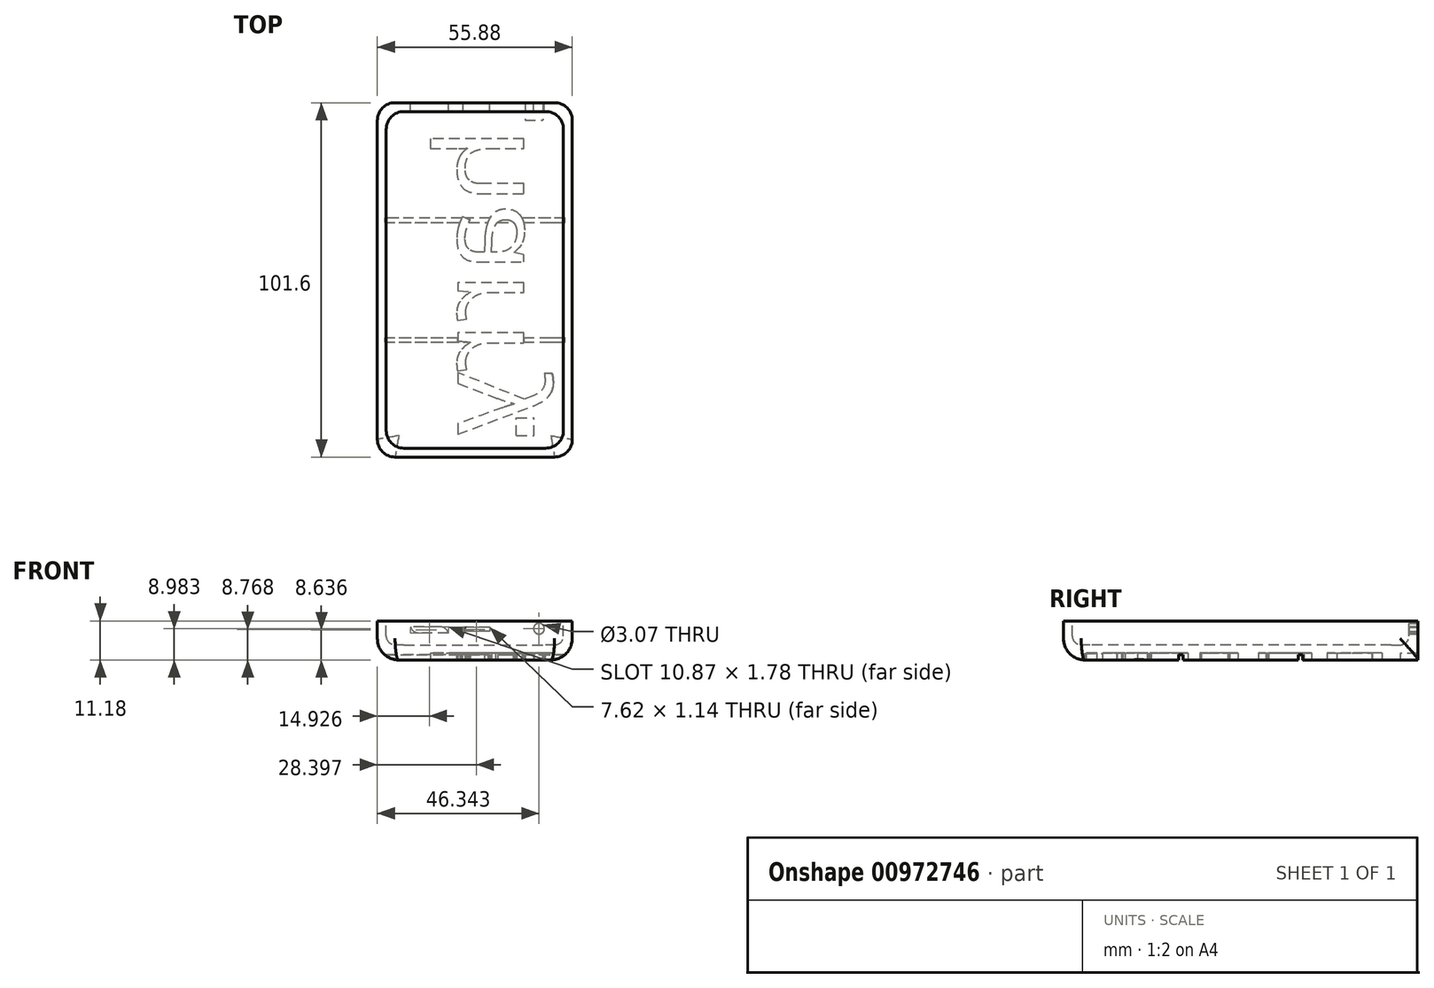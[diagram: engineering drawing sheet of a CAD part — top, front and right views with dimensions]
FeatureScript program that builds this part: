
annotation { "Feature Type Name" : "Feature", "Feature Type Description" : "" }
export const myFeature = defineFeature(function(context is Context, id is Id, definition is map)
    precondition{}
    {
        {
            var Q0;
            Q0=qCreatedBy(makeId("Top.planeOp"),FACE);
            var sketch = newSketch(context, id + "F0", { "sketchPlane" : qUnion([Q0])});
            skLineSegment(sketch, "E0.bottom", {"start": v(-45.15, 60.21) * mm, "end": v(10.73, 60.21) * mm});
            skLineSegment(sketch, "E0.top", {"start": v(-45.15, -41.39) * mm, "end": v(10.73, -41.39) * mm});
            skLineSegment(sketch, "E0.left", {"start": v(-45.15, 60.21) * mm, "end": v(-45.15, -41.39) * mm});
            skLineSegment(sketch, "E0.right", {"start": v(10.73, 60.21) * mm, "end": v(10.73, -41.39) * mm});
            skSolve(sketch);
        }
        {
            var Q0;
            Q0 = qSketchRegion(id + "F0", true);
            extrude(context, id + "F1", {"entities" : qUnion([Q0]), "oppositeDirection" : true, "depth" : 9.65 * mm, "offsetDistance" : 25.4 * mm});
        }
        {
            var Q0;
            Q0=makeQuery(id+"F1.opExtrude","CAP_FACE",FACE,{"disambiguationData":[OSD([sQuery(id+"F0.wireOp",EDGE,"E0.bottom"),sQuery(id+"F0.wireOp",EDGE,"E0.top"),sQuery(id+"F0.wireOp",EDGE,"E0.left"),sQuery(id+"F0.wireOp",EDGE,"E0.right")])],"isStart":true});
            var sketch = newSketch(context, id + "F2", { "sketchPlane" : qUnion([Q0])});
            skLineSegment(sketch, "E1.bottom", {"start": v(-42.6, 57.67) * mm, "end": v(8.2, 57.67) * mm});
            skLineSegment(sketch, "E1.top", {"start": v(-42.6, -38.85) * mm, "end": v(8.2, -38.85) * mm});
            skLineSegment(sketch, "E1.left", {"start": v(-42.6, 57.67) * mm, "end": v(-42.6, -38.85) * mm});
            skLineSegment(sketch, "E1.right", {"start": v(8.2, 57.67) * mm, "end": v(8.2, -38.85) * mm});
            skSolve(sketch);
        }
        {
            var Q0;
            Q0 = qSketchRegion(id + "F2", true);
            extrude(context, id + "F3", {"entities" : qUnion([Q0]), "operationType" : NewBodyOperationType.REMOVE, "oppositeDirection" : true, "depth" : 6.86 * mm, "offsetDistance" : 25.4 * mm});
        }
        {
            var Q0;
            Q0=makeQuery(id+"F1.opExtrude","CAP_FACE",FACE,{"disambiguationData":[OSD([sQuery(id+"F0.wireOp",EDGE,"E0.bottom"),sQuery(id+"F0.wireOp",EDGE,"E0.top"),sQuery(id+"F0.wireOp",EDGE,"E0.left"),sQuery(id+"F0.wireOp",EDGE,"E0.right")])],"isStart":false});
            var sketch = newSketch(context, id + "F4", { "sketchPlane" : qUnion([Q0])});
            skLineSegment(sketch, "E2.bottom", {"start": v(10.73, -60.21) * mm, "end": v(-45.15, -60.21) * mm});
            skLineSegment(sketch, "E2.top", {"start": v(10.73, -27.2) * mm, "end": v(-45.15, -27.2) * mm});
            skLineSegment(sketch, "E2.left", {"start": v(10.73, -60.21) * mm, "end": v(10.73, -27.2) * mm});
            skLineSegment(sketch, "E2.right", {"start": v(-45.15, -60.21) * mm, "end": v(-45.15, -27.2) * mm});
            skLineSegment(sketch, "E3.bottom", {"start": v(-45.15, 41.39) * mm, "end": v(10.73, 41.39) * mm});
            skLineSegment(sketch, "E3.top", {"start": v(-45.15, 8.37) * mm, "end": v(10.73, 8.37) * mm});
            skLineSegment(sketch, "E3.left", {"start": v(-45.15, 41.39) * mm, "end": v(-45.15, 8.37) * mm});
            skLineSegment(sketch, "E3.right", {"start": v(10.73, 41.39) * mm, "end": v(10.73, 8.37) * mm});
            skLineSegment(sketch, "E4.bottom", {"start": v(-45.15, 7.1) * mm, "end": v(10.73, 7.1) * mm});
            skLineSegment(sketch, "E4.top", {"start": v(-45.15, -25.92) * mm, "end": v(10.73, -25.92) * mm});
            skLineSegment(sketch, "E4.left", {"start": v(-45.15, 7.1) * mm, "end": v(-45.15, -25.92) * mm});
            skLineSegment(sketch, "E4.right", {"start": v(10.73, 7.1) * mm, "end": v(10.73, -25.92) * mm});
            skSolve(sketch);
        }
        {
            var Q0;
            Q0 = qSketchRegion(id + "F4", true);
            extrude(context, id + "F5", {"entities" : qUnion([Q0]), "operationType" : NewBodyOperationType.ADD, "depth" : 1.52 * mm, "offsetDistance" : 25.4 * mm});
        }
        {
            var Q0;
            Q0=makeQuery(id+"F5.opExtrude","CAP_FACE",FACE,{"disambiguationData":[OSD([sQuery(id+"F4.wireOp",EDGE,"E3.bottom"),sQuery(id+"F4.wireOp",EDGE,"E3.top"),sQuery(id+"F4.wireOp",EDGE,"E3.left"),sQuery(id+"F4.wireOp",EDGE,"E3.right")])],"isStart":false});
            cPlane(context, id + "F6", {"entities" : qUnion([Q0]), "cplaneType" : CPlaneType.OFFSET, "offset" : 0 * mm, "width" : 152.4 * mm, "height" : 152.4 * mm});
        }
        {
            var Q0;
            Q0=qCreatedBy(id+"F6.planeOp",FACE);
            var sketch = newSketch(context, id + "F7", { "sketchPlane" : qUnion([Q0])});
            skText(sketch, "E5", { "text": "harry", "fontName": "OpenSans-Regular.ttf"});
            const initialGuessF7  = {"E5": [-0.00318, -0.05294, 0, 1, 0.0254]};
            skSetInitialGuess(sketch, initialGuessF7);
            skSolve(sketch);
        }
        {
            var Q0;
            Q0 = qSketchRegion(id + "F7", true);
            extrude(context, id + "F8", {"entities" : qUnion([Q0]), "operationType" : NewBodyOperationType.REMOVE, "oppositeDirection" : true, "depth" : 2.03 * mm, "offsetDistance" : 25.4 * mm});
        }
        {
            var Q0;
            Q0=makeQuery(id+"F3.boolean.opBoolean","COPY",EDGE,{"derivedFrom":makeQuery(id+"F3.opExtrude","SWEPT_EDGE",EDGE,{"disambiguationData":[OSD([sQuery(id+"F2.wireOp",EDGE,"E1.bottom"),sQuery(id+"F2.wireOp",EDGE,"E1.right")])]})});
            var Q1;
            Q1=makeQuery(id+"F3.boolean.opBoolean","COPY",EDGE,{"derivedFrom":makeQuery(id+"F3.opExtrude","SWEPT_EDGE",EDGE,{"disambiguationData":[OSD([sQuery(id+"F2.wireOp",EDGE,"E1.bottom"),sQuery(id+"F2.wireOp",EDGE,"E1.left")])]})});
            var Q2;
            Q2=makeQuery(id+"F3.boolean.opBoolean","COPY",EDGE,{"derivedFrom":makeQuery(id+"F3.opExtrude","SWEPT_EDGE",EDGE,{"disambiguationData":[OSD([sQuery(id+"F2.wireOp",EDGE,"E1.top"),sQuery(id+"F2.wireOp",EDGE,"E1.left")])]})});
            var Q3;
            Q3=makeQuery(id+"F3.boolean.opBoolean","COPY",EDGE,{"derivedFrom":makeQuery(id+"F3.opExtrude","SWEPT_EDGE",EDGE,{"disambiguationData":[OSD([sQuery(id+"F2.wireOp",EDGE,"E1.top"),sQuery(id+"F2.wireOp",EDGE,"E1.right")])]})});
            var Q4;
            Q4=makeQuery(id+"F5.boolean.opBoolean","MERGE",EDGE,{"derivedFrom":[makeQuery(id+"F1.opExtrude","SWEPT_EDGE",EDGE,{"disambiguationData":[OSD([sQuery(id+"F0.wireOp",EDGE,"E0.bottom"),sQuery(id+"F0.wireOp",EDGE,"E0.left")])]}),makeQuery(id+"F5.opExtrude","SWEPT_EDGE",EDGE,{"disambiguationData":[OSD([sQuery(id+"F4.wireOp",EDGE,"E2.bottom"),sQuery(id+"F4.wireOp",EDGE,"E2.right")])]})]});
            var Q5;
            Q5=makeQuery(id+"F5.boolean.opBoolean","MERGE",EDGE,{"derivedFrom":[makeQuery(id+"F1.opExtrude","SWEPT_EDGE",EDGE,{"disambiguationData":[OSD([sQuery(id+"F0.wireOp",EDGE,"E0.bottom"),sQuery(id+"F0.wireOp",EDGE,"E0.right")])]}),makeQuery(id+"F5.opExtrude","SWEPT_EDGE",EDGE,{"disambiguationData":[OSD([sQuery(id+"F4.wireOp",EDGE,"E2.bottom"),sQuery(id+"F4.wireOp",EDGE,"E2.left")])]})]});
            var Q6;
            Q6=makeQuery(id+"F5.boolean.opBoolean","MERGE",EDGE,{"derivedFrom":[makeQuery(id+"F1.opExtrude","SWEPT_EDGE",EDGE,{"disambiguationData":[OSD([sQuery(id+"F0.wireOp",EDGE,"E0.top"),sQuery(id+"F0.wireOp",EDGE,"E0.left")])]}),makeQuery(id+"F5.opExtrude","SWEPT_EDGE",EDGE,{"disambiguationData":[OSD([sQuery(id+"F4.wireOp",EDGE,"E3.bottom"),sQuery(id+"F4.wireOp",EDGE,"E3.left")])]})]});
            var Q7;
            Q7=makeQuery(id+"F5.boolean.opBoolean","MERGE",EDGE,{"derivedFrom":[makeQuery(id+"F1.opExtrude","SWEPT_EDGE",EDGE,{"disambiguationData":[OSD([sQuery(id+"F0.wireOp",EDGE,"E0.top"),sQuery(id+"F0.wireOp",EDGE,"E0.right")])]}),makeQuery(id+"F5.opExtrude","SWEPT_EDGE",EDGE,{"disambiguationData":[OSD([sQuery(id+"F4.wireOp",EDGE,"E3.bottom"),sQuery(id+"F4.wireOp",EDGE,"E3.right")])]})]});
            fillet(context, id + "F9", {"entities" : qUnion([Q0, Q1, Q2, Q3, Q4, Q5, Q6, Q7]), "radius" : 5.08 * mm, "tangentPropagation" : true, "allowEdgeOverflow" : false});
        }
        {
            var Q0;
            Q0=makeQuery(id+"F3.boolean.opBoolean","COPY",EDGE,{"derivedFrom":makeQuery(id+"F3.opExtrude","CAP_EDGE",EDGE,{"disambiguationData":[OSD([sQuery(id+"F2.wireOp",EDGE,"E1.right")])],"isStart":false})});
            fillet(context, id + "F10", {"entities" : qUnion([Q0]), "radius" : 2.54 * mm, "tangentPropagation" : true, "allowEdgeOverflow" : false});
        }
        {
            var Q0;
            Q0=makeQuery(id+"F5.opExtrude","CAP_EDGE",EDGE,{"disambiguationData":[OSD([sQuery(id+"F4.wireOp",EDGE,"E3.right")])],"isStart":false});
            fillet(context, id + "F11", {"entities" : qUnion([Q0]), "radius" : 6.13 * mm, "tangentPropagation" : true, "allowEdgeOverflow" : false});
        }
        {
            var Q0;
            Q0=makeQuery(id+"F5.boolean.opBoolean","MERGE",FACE,{"derivedFrom":[makeQuery(id+"F1.opExtrude","SWEPT_FACE",FACE,{"disambiguationData":[OSD([sQuery(id+"F0.wireOp",EDGE,"E0.bottom")])]}),makeQuery(id+"F5.opExtrude","SWEPT_FACE",FACE,{"disambiguationData":[OSD([sQuery(id+"F4.wireOp",EDGE,"E2.bottom")])]})]});
            var sketch = newSketch(context, id + "F12", { "sketchPlane" : qUnion([Q0])});
            skCircle(sketch, "E6", {"center": v(-1.2, -2.2) * mm, "radius": 1.54 * mm});
            skSolve(sketch);
        }
        {
            var Q0;
            Q0 = qSketchRegion(id + "F12", true);
            extrude(context, id + "F13", {"entities" : qUnion([Q0]), "operationType" : NewBodyOperationType.REMOVE, "oppositeDirection" : true, "depth" : 25.4 * mm, "offsetDistance" : 25.4 * mm});
        }
        {
            var Q0;
            Q0=makeQuery(id+"F5.boolean.opBoolean","MERGE",FACE,{"derivedFrom":[makeQuery(id+"F1.opExtrude","SWEPT_FACE",FACE,{"disambiguationData":[OSD([sQuery(id+"F0.wireOp",EDGE,"E0.bottom")])]}),makeQuery(id+"F5.opExtrude","SWEPT_FACE",FACE,{"disambiguationData":[OSD([sQuery(id+"F4.wireOp",EDGE,"E2.bottom")])]})]});
            var sketch = newSketch(context, id + "F14", { "sketchPlane" : qUnion([Q0])});
            skLineSegment(sketch, "E7.bottom", {"start": v(12.94, -1.84) * mm, "end": v(20.56, -1.84) * mm});
            skLineSegment(sketch, "E7.top", {"start": v(12.94, -2.98) * mm, "end": v(20.56, -2.98) * mm});
            skLineSegment(sketch, "E7.left", {"start": v(12.94, -1.84) * mm, "end": v(12.94, -2.98) * mm});
            skLineSegment(sketch, "E7.right", {"start": v(20.56, -1.84) * mm, "end": v(20.56, -2.98) * mm});
            skSolve(sketch);
        }
        {
            var Q0;
            Q0 = qSketchRegion(id + "F14", true);
            extrude(context, id + "F15", {"entities" : qUnion([Q0]), "operationType" : NewBodyOperationType.REMOVE, "oppositeDirection" : true, "depth" : 25.4 * mm, "offsetDistance" : 25.4 * mm});
        }
        {
            var Q0;
            Q0=makeQuery(id+"F5.boolean.opBoolean","MERGE",FACE,{"derivedFrom":[makeQuery(id+"F1.opExtrude","SWEPT_FACE",FACE,{"disambiguationData":[OSD([sQuery(id+"F0.wireOp",EDGE,"E0.bottom")])]}),makeQuery(id+"F5.opExtrude","SWEPT_FACE",FACE,{"disambiguationData":[OSD([sQuery(id+"F4.wireOp",EDGE,"E2.bottom")])]})]});
            var sketch = newSketch(context, id + "F16", { "sketchPlane" : qUnion([Q0])});
            skLineSegment(sketch, "E8.bottom", {"start": v(24.79, -1.66) * mm, "end": v(35.66, -1.66) * mm});
            skLineSegment(sketch, "E8.top", {"start": v(24.79, -3.43) * mm, "end": v(35.66, -3.43) * mm});
            skLineSegment(sketch, "E8.left", {"start": v(24.79, -1.66) * mm, "end": v(24.79, -3.43) * mm});
            skLineSegment(sketch, "E8.right", {"start": v(35.66, -1.66) * mm, "end": v(35.66, -3.43) * mm});
            skSolve(sketch);
        }
        {
            var Q0;
            Q0 = qSketchRegion(id + "F16", true);
            extrude(context, id + "F17", {"entities" : qUnion([Q0]), "operationType" : NewBodyOperationType.REMOVE, "oppositeDirection" : true, "depth" : 25.4 * mm, "offsetDistance" : 25.4 * mm});
        }
        {
            var Q0;
            Q0=makeQuery(id+"F17.boolean.opBoolean","COPY",EDGE,{"derivedFrom":makeQuery(id+"F17.opExtrude","SWEPT_EDGE",EDGE,{"disambiguationData":[OSD([sQuery(id+"F16.wireOp",EDGE,"E8.bottom"),sQuery(id+"F16.wireOp",EDGE,"E8.left")])]})});
            var Q1;
            Q1=makeQuery(id+"F17.boolean.opBoolean","COPY",EDGE,{"derivedFrom":makeQuery(id+"F17.opExtrude","SWEPT_EDGE",EDGE,{"disambiguationData":[OSD([sQuery(id+"F16.wireOp",EDGE,"E8.top"),sQuery(id+"F16.wireOp",EDGE,"E8.right")])]})});
            fillet(context, id + "F18", {"entities" : qUnion([Q0, Q1]), "radius" : 2.5 * mm, "tangentPropagation" : true, "allowEdgeOverflow" : false});
        }
        {
            var Q0;
            Q0=makeQuery(id+"F5.opExtrude","CAP_FACE",FACE,{"disambiguationData":[OSD([sQuery(id+"F4.wireOp",EDGE,"E3.bottom"),sQuery(id+"F4.wireOp",EDGE,"E3.top"),sQuery(id+"F4.wireOp",EDGE,"E3.left"),sQuery(id+"F4.wireOp",EDGE,"E3.right")])],"isStart":false});
            var sketch = newSketch(context, id + "F19", { "sketchPlane" : qUnion([Q0])});
            skLineSegment(sketch, "E9.bottom", {"start": v(-5.26, 35.26) * mm, "end": v(-0.18, 35.26) * mm});
            skLineSegment(sketch, "E9.top", {"start": v(-5.26, 30.18) * mm, "end": v(-0.18, 30.18) * mm});
            skLineSegment(sketch, "E9.left", {"start": v(-5.26, 35.26) * mm, "end": v(-5.26, 30.18) * mm});
            skLineSegment(sketch, "E9.right", {"start": v(-0.18, 35.26) * mm, "end": v(-0.18, 30.18) * mm});
            skLineSegment(sketch, "E10.bottom", {"start": v(-2.82, -60.24) * mm, "end": v(2.26, -60.24) * mm});
            skLineSegment(sketch, "E10.top", {"start": v(-2.82, -55.16) * mm, "end": v(2.26, -55.16) * mm});
            skLineSegment(sketch, "E10.left", {"start": v(-2.82, -60.24) * mm, "end": v(-2.82, -55.16) * mm});
            skLineSegment(sketch, "E10.right", {"start": v(2.26, -60.24) * mm, "end": v(2.26, -55.16) * mm});
            skSolve(sketch);
        }
        {
            var Q0;
            Q0 = qSketchRegion(id + "F19", true);
            extrude(context, id + "F20", {"entities" : qUnion([Q0]), "operationType" : NewBodyOperationType.REMOVE, "oppositeDirection" : true, "depth" : 1.83 * mm, "offsetDistance" : 25.4 * mm});
        }
    });
